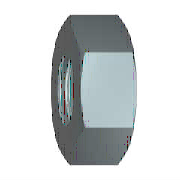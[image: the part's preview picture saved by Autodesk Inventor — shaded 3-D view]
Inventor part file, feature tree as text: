
AUTODESK INVENTOR PART (.ipt)
format: ipt  version: 2020 (Build 240168000, 168)  size: 165,888 bytes
history: native  units: mm (DEFAULTED — no unit token found)
features: sketch x3, other x2, extrude x1, hole x1, plane x1
ambient origin geometry x7: Origin, YZ Plane, XZ Plane, X Axis, Y Axis, Z Axis, Center Point
bodies: Solid1 (feature_tree)
feature tree (8):
  extrude  "Bryła"  Depth=9.237604mm
  other  "Faza1"
  hole  "Gwint"  [1 undecoded]
  other  "Work Axis1"
  plane  "Work Plane1"
  sketch  "Szkic1"
  sketch  "Szkic2"
  sketch  "Szkic3"
note: 1 required parameter value undecoded (feature->parameter linkage not recoverable at this tier; creation-order binding heuristic only, values carry confidence <= 0.55)
